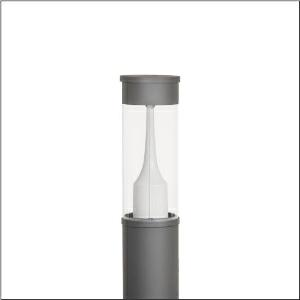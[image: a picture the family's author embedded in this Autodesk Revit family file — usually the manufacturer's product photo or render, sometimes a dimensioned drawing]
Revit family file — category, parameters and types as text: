
# Revit family: city-light_120_iq___p1_0a_5xa5285nf14h_00f5
name_source: partatom
category: Lighting Fixtures
units: mm (PartAtom-declared; Revit-internal decimal feet)

## family parameters
Cut with Voids When Loaded = No
Host = Face
Light Source = No
Part Type = Normal
Room Calculation Point = No
Round Connector Dimension = Use Diameter
Shared = No

## types (1)
- --- (1 x LED, 1510 lm, 11.8 W, 2700K)
    Apparent Load = 12 VA
    CIE Flux Codes = 32 61 90 93 100
    Color Rendering = 70
    Color Temperature = 2700K
    Default Elevation = 1800 mm
    Description = City-Light 120 iQ, bollard luminaire, Module 540 iQ-SR, primary light control with 3 zone facetted reflector, of plastic, silver coated, highly specular, structured, primary optical cover: cover, of PMMA, transparent, partly coated, light distribution: P1.0a, primary light characteristic: strongly asymmetric, LED, High Power LED, rated luminous flux: 1.510lm, luminous efficacy: 128lm/W, light colour: 727, colour temperature: 2700K, control gear: ECG iQ, control: presetting dimming logarithmic, Street-Remote, Auto-Match, Temp-Guard, Lumen-Switch, Night-Set, Smart-Wire, Light-Fading, Desk-Remote (wireless, voltage-free reading and setting of iQ features in the workshop via application-optimized NFC function/RFID function), optimised constant luminous flux control (CLO 2.0), with terminal, 6-pole, max. 2.5mm², mains connection: 230..240V, AC, 50/60Hz, start of lifetime: 12W, end of service life: 12W, reduction: 6W, luminaire housing, cylindrical, of extruded aluminium section, coated, Siteco® metallic grey (DB 702S), length: 1.200mm, diameter: 200mm, Module 540 iQ-SR, traffic white (RAL 9016), equipment: standard, protection rating (complete): IP54, insulation class (complete): insulation class II (safety insulation), certification: CE, ENEC, VDE, packaging unit: 1 piece

Light Distribution: P1.0a
    Height = 500 mm
    Lamp = 1 x LED
    Lamp Light Flux = 1510 lm
    Lamp Power = 11.8 W
    Lamp count = 1
    Length = 200 mm  [stored 0.656168 ft]
    Luminous efficacy = 128 lm/W
    Manufacturer = Siteco
    ModVariant = No
    Model = 5XA5285NF14H
    Mounting Place = Floor
    Mounting Type = Freestanding
    Number of Poles = 1
    OnlyDefault = Yes
    Power Factor = 1
    Product Name = City-Light 120 iQ | P1.0a
    Product group = bollard luminaire
    ProductGroupID = 1304
    Protection Class = Protection class II
    Protection Degree = IP 54
    RLX_Detail_Level = 1
    RLX_Emergency_Light_Flux = 0 lm
    RLX_Emergency_Type = 0
    RLX_Emergency_Type_DB = No
    RlxData = <blob elided: 52797 chars, md5=3849e3e8>
    Socket = socket
    Standby Power = 0 W
    System Light Flux = 1510 lm
    System Power = 12 W
    Type Comments = factory setting: luminous flux: 100 % | dim-lin: 254 | 472 mA
    Type Image = l_1006922.jpg
    URL = http://relux.com
    VarID = @adj_103339
    Voltage = 0 V
    Weight = 0.00 kg
    Width = 0 mm  [stored 0 ft]

note: [stored X ft] marks values corroborated as IEEE doubles in the binary element streams (Revit-internal decimal feet)

## geometry (parser evidence)
native form markers: Blend x4, Sweep x12
no freeform markers — native parametric forms only
